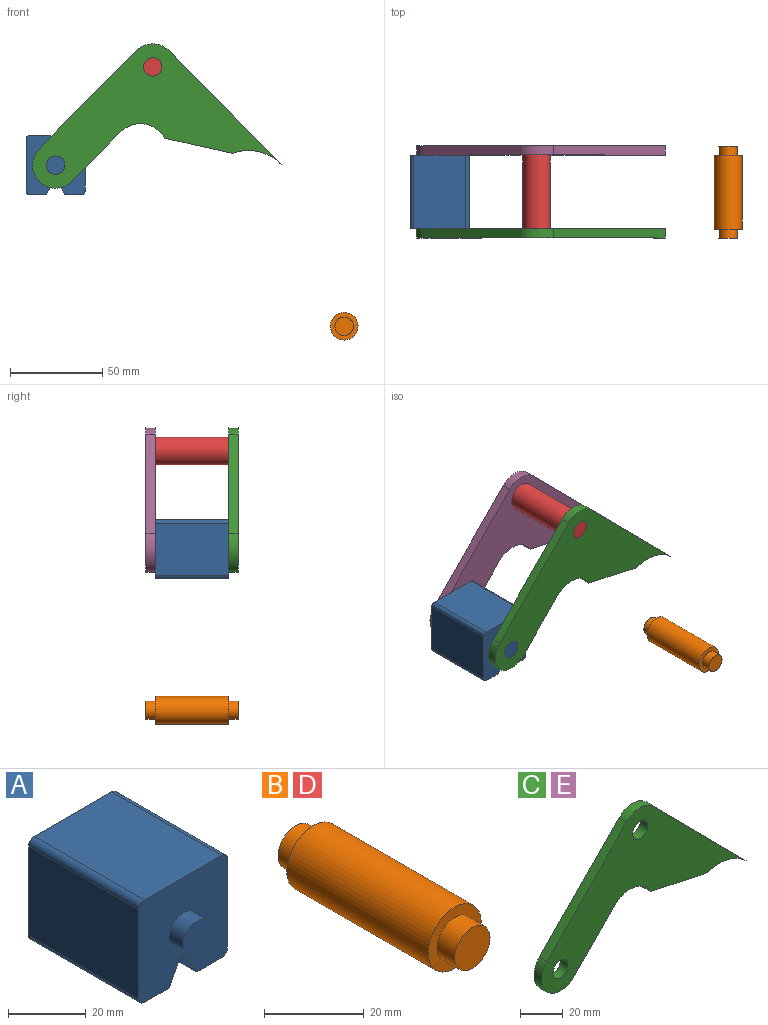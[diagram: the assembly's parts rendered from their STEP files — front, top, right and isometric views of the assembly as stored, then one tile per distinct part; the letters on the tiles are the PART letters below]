
ASSEMBLY  parts=5 mates=3
PART A: 18 faces, bbox 32.1x50x32.1 mm
  f0: plane 40x28.08mm, normal (1,0,0), area 1123.1mm2, adj f4,f10,f13,f14
  f1: plane 40x9.04mm, normal (0,0,-1), area 361.6mm2, adj f2,f4,f10,f14
  f2: plane 40x6.42mm, normal (-0.89,0,-0.45), area 287.2mm2, adj f1,f4,f10,f15
  f3: plane 40x6.42mm, normal (0.89,0,-0.45), area 287.2mm2, adj f4,f5,f10,f15
  f4: plane 32.08x32.08mm, normal (0,-1,0), area 900.6mm2, adj f0,f1,f2,f3,f5,f6,f7,f9
  f5: plane 40x9.04mm, normal (0,0,-1), area 361.6mm2, adj f3,f4,f10,f16
  f6: plane 40x28.08mm, normal (0,0,1), area 1123.1mm2, adj f4,f10,f13,f17
  f7: plane 40x28.08mm, normal (-1,0,0), area 1123.1mm2, adj f4,f10,f16,f17
  f8: plane 10x10mm, normal (0,-1,0), area 78.5mm2, adj f9
  f9: cylinder r=5mm len=10mm, axis (0,1,0), area 157.1mm2, adj f4,f8
  f10: plane 32.08x32.08mm, normal (0,1,0), area 900.6mm2, adj f0,f1,f2,f3,f5,f6,f7,f12
  f11: plane 10x10mm, normal (0,1,0), area 78.5mm2, adj f12
  f12: cylinder r=5mm len=10mm, axis (0,-1,0), area 157.1mm2, adj f10,f11
  f13: cylinder r=2mm len=40mm, axis (0,1,0), area 125.7mm2, adj f0,f4,f6,f10
  f14: cylinder r=2mm len=40mm, axis (0,-1,0), area 125.7mm2, adj f0,f1,f4,f10
  f15: cylinder r=2mm len=40mm, axis (0,1,0), area 177.1mm2, adj f2,f3,f4,f10
  f16: cylinder r=2mm len=40mm, axis (0,1,0), area 125.7mm2, adj f4,f5,f7,f10
  f17: cylinder r=2mm len=40mm, axis (0,-1,0), area 125.7mm2, adj f4,f6,f7,f10
PART B: 7 faces, bbox 15x50x15 mm
  f0: cylinder r=7.5mm len=40mm, axis (0,-1,0), area 1885mm2, adj f2,f5
  f1: cylinder r=5mm len=10mm, axis (0,1,0), area 157.1mm2, adj f2,f3
  f2: plane 15x15mm, normal (0,-1,0), area 98.2mm2, adj f0,f1
  f3: plane 10x10mm, normal (0,-1,0), area 78.5mm2, adj f1
  f4: cylinder r=5mm len=10mm, axis (0,-1,0), area 157.1mm2, adj f5,f6
  f5: plane 15x15mm, normal (0,1,0), area 98.2mm2, adj f0,f4
  f6: plane 10x10mm, normal (0,1,0), area 78.5mm2, adj f4
PART C: 12 faces, bbox 135x5x78.4 mm
  f0: plane 53.35x52.71mm, normal (-0.71,0,0.7), area 375mm2, adj f1,f8,f10,f11
  f1: cylinder r=12.5mm len=21.39mm, axis (0,1,0), area 196.3mm2, adj f0,f2,f10,f11
  f2: plane 26.86x26.54mm, normal (0.71,0,-0.7), area 188.8mm2, adj f1,f3,f10,f11
  f3: cylinder r=15mm len=23.89mm, axis (0,1,0), area 140.2mm2, adj f2,f4,f10,f11
  f4: plane 36.75x8.2mm, normal (-0.22,0,-0.98), area 188.3mm2, adj f3,f5,f10,f11
  f5: cylinder r=25mm len=26.41mm, axis (0,1,0), area 143mm2, adj f4,f6,f10,f11
  f6: plane 61.6x60.87mm, normal (0.71,0,0.7), area 433mm2, adj f5,f8,f10,f11
  f7: cylinder r=5mm len=10mm, axis (0,1,0), area 157.1mm2, adj f10,f11
  f8: cylinder r=12.5mm len=17.78mm, axis (0,1,0), area 98.9mm2, adj f0,f6,f10,f11
  f9: cylinder r=5mm len=10mm, axis (0,1,0), area 157.1mm2, adj f10,f11
  f10: plane 134.97x78.35mm, normal (0,-1,0), area 3847.2mm2, adj f0,f1,f2,f3,f4,f5,f6,f7
  f11: plane 134.97x78.35mm, normal (0,1,0), area 3847.2mm2, adj f0,f1,f2,f3,f4,f5,f6,f7
PART D: same geometry as B
PART E: same geometry as C
PLACE A t=(0,-20,0)mm
PLACE B t=(103.95,-20,-140.78)mm
PLACE C t=(0,-20,0)mm fixed
PLACE D t=(0,-20,0)mm
PLACE E t=(0,25,0)mm
MATE fastened E.f7 <-> D.f0  axis (0,-1,0) through (-51.98,20,70.39)mm
MATE revolute A.f9 <-> C.f1  axis (0,-1,0) through (-104.69,-25,17.04)mm
MATE fastened B.f0 <-> C.f11  axis (0,-1,0) through (51.98,-20,-70.39)mm
